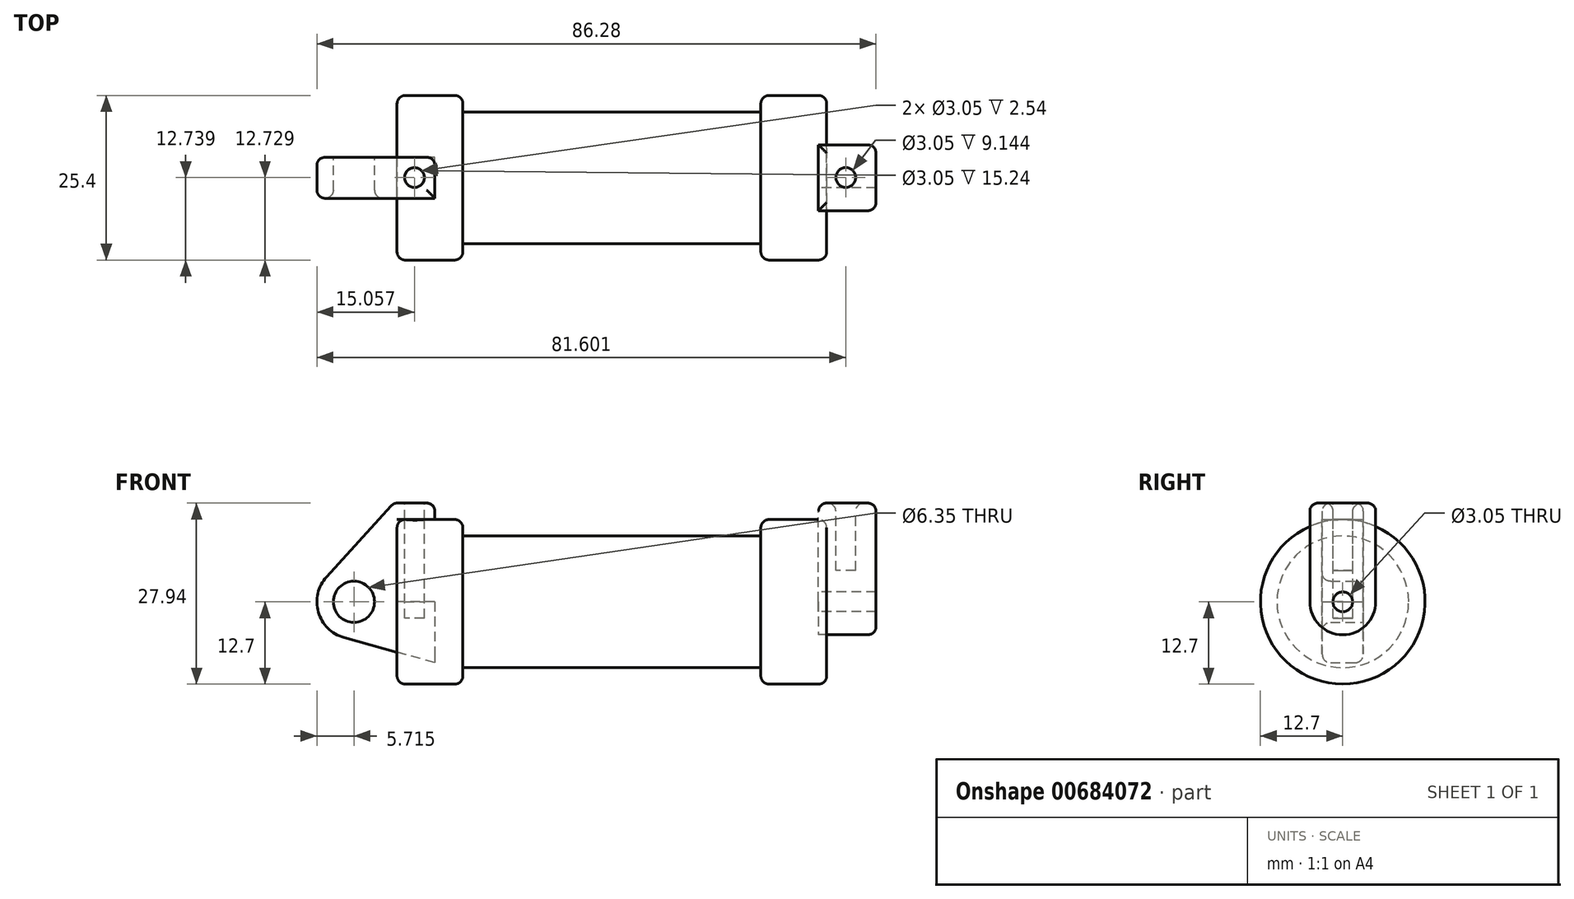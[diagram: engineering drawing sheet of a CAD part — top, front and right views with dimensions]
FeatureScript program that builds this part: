
annotation { "Feature Type Name" : "Feature", "Feature Type Description" : "" }
export const myFeature = defineFeature(function(context is Context, id is Id, definition is map)
    precondition{}
    {
        {
            var Q0;
            Q0=qCreatedBy(makeId("Front.planeOp"),FACE);
            var sketch = newSketch(context, id + "F0", { "sketchPlane" : qUnion([Q0])});
            skLineSegment(sketch, "E0", {"start": v(0, 0) * mm, "end": v(0, 12.7) * mm});
            skLineSegment(sketch, "E1", {"start": v(0, 12.7) * mm, "end": v(10.16, 12.7) * mm});
            skLineSegment(sketch, "E2", {"start": v(10.16, 12.7) * mm, "end": v(10.16, 10.16) * mm});
            skLineSegment(sketch, "E3", {"start": v(10.16, 10.16) * mm, "end": v(56.13, 10.16) * mm});
            skLineSegment(sketch, "E4", {"start": v(56.13, 10.16) * mm, "end": v(56.13, 12.7) * mm});
            skLineSegment(sketch, "E5", {"start": v(56.13, 12.7) * mm, "end": v(66.3, 12.7) * mm});
            skLineSegment(sketch, "E6", {"start": v(66.3, 12.7) * mm, "end": v(66.3, 0) * mm});
            skLineSegment(sketch, "E7", {"start": v(66.3, 0) * mm, "end": v(0, 0) * mm});
            skLineSegment(sketch, "E8", {"start": v(5.84, 15.24) * mm, "end": v(-0.5, 15.24) * mm});
            skLineSegment(sketch, "E9", {"start": v(-0.5, 15.24) * mm, "end": v(-10.88, 3.85) * mm});
            skLineSegment(sketch, "E10", {"start": v(0, 0) * mm, "end": v(-6.65, 0) * mm});
            skCircle(sketch, "E11", {"center": v(-6.65, 0) * mm, "radius": 5.72 * mm});
            skCircle(sketch, "E12", {"center": v(-6.65, 0) * mm, "radius": 3.18 * mm});
            skLineSegment(sketch, "E13", {"start": v(5.84, 15.24) * mm, "end": v(5.84, -9.4) * mm});
            skLineSegment(sketch, "E14", {"start": v(5.84, -9.4) * mm, "end": v(-8.18, -5.5) * mm});
            skText(sketch, "E15", { "text": "volume\n1.706 ^3", "fontName": "OpenSans-Regular.ttf"});
            const initialGuessF0  = {"E15": [0.00013, 0.0607, 1, 0, 0.01304]};
            skSetInitialGuess(sketch, initialGuessF0);
            skSolve(sketch);
        }
        {
            var Q0;
            {var subQ0=sQuery(id+"F0.wireOp",EDGE,"E2");Q0=makeQuery(id+"F0.imprint","IMPRINT",FACE,{"disambiguationData":[TD([[makeQuery(id+"F0.imprint","IMPRINT",EDGE,{"derivedFrom":subQ0}),-1.0]])]});}
            var Q1;
            {var subQ0=sQuery(id+"F0.wireOp",EDGE,"E0");Q1=makeQuery(id+"F0.imprint","IMPRINT",FACE,{"disambiguationData":[TD([[makeQuery(id+"F0.imprint","IMPRINT",EDGE,{"derivedFrom":subQ0}),-1.0]])]});}
            var Q2;
            Q2=sQuery(id+"F0.wireOp",EDGE,"E7");
            revolve(context, id + "F1", {"entities" : qUnion([Q0, Q1]), "axis" : qUnion([Q2]), "revolveType" : RevolveType.FULL});
        }
        {
            var Q0;
            {var subQ1=sQuery(id+"F0.wireOp",EDGE,"E0");Q0=makeQuery(id+"F0.imprint","IMPRINT",FACE,{"disambiguationData":[TD([[makeQuery(id+"F0.imprint","IMPRINT",EDGE,{"derivedFrom":subQ1}),1.0]])]});}
            var Q1;
            {var subQ0=sQuery(id+"F0.wireOp",EDGE,"E14");Q1=makeQuery(id+"F0.imprint","IMPRINT",FACE,{"disambiguationData":[TD([[makeQuery(id+"F0.imprint","IMPRINT",EDGE,{"derivedFrom":subQ0}),-1.0]])]});}
            var Q2;
            {var subQ5=sQuery(id+"F0.wireOp",EDGE,"E12");Q2=makeQuery(id+"F0.imprint","IMPRINT",FACE,{"disambiguationData":[TD([[makeQuery(id+"F0.imprint","IMPRINT",EDGE,{"derivedFrom":subQ5}),-1.0]])]});}
            extrude(context, id + "F2", {"entities" : qUnion([Q0, Q1, Q2]), "endBound" : BoundingType.SYMMETRIC, "depth" : 6.35 * mm, "offsetDistance" : 25.4 * mm});
        }
        {
            var Q0;
            Q0=makeQuery(id+"F1.opRevolve","SWEPT_FACE",FACE,{"disambiguationData":[OSD([sQuery(id+"F0.wireOp",EDGE,"E6")])]});
            var sketch = newSketch(context, id + "F3", { "sketchPlane" : qUnion([Q0])});
            skCircle(sketch, "E16", {"center": v(0, 0) * mm, "radius": 1.52 * mm});
            skCircle(sketch, "E17", {"center": v(0, 0) * mm, "radius": 5.08 * mm});
            skLineSegment(sketch, "E18", {"start": v(-5.08, 0) * mm, "end": v(-5.08, 15.24) * mm});
            skLineSegment(sketch, "E19", {"start": v(5.08, 0) * mm, "end": v(5.08, 15.24) * mm});
            skLineSegment(sketch, "E20", {"start": v(-5.08, 15.24) * mm, "end": v(5.08, 15.24) * mm});
            skSolve(sketch);
        }
        {
            var Q0;
            Q0 = qSketchRegion(id + "F3", true);
            extrude(context, id + "F4", {"entities" : qUnion([Q0]), "depth" : 7.62 * mm, "offsetDistance" : 25.4 * mm, "hasSecondDirection" : true, "secondDirectionOppositeDirection" : true, "secondDirectionDepth" : 1.27 * mm});
        }
        {
            var Q0;
            Q0=makeQuery(id+"F4.opExtrude","SWEPT_FACE",FACE,{"disambiguationData":[OSD([sQuery(id+"F3.wireOp",EDGE,"E20")])]});
            var sketch = newSketch(context, id + "F5", { "sketchPlane" : qUnion([Q0])});
            skCircle(sketch, "E21", {"center": v(69.23, 0.04) * mm, "radius": 1.52 * mm});
            skSolve(sketch);
        }
        {
            var Q0;
            Q0=makeQuery(id+"F5.imprint","IMPRINT",FACE,{"disambiguationData":[TD([[makeQuery(id+"F5.imprint","IMPRINT",EDGE,{"derivedFrom":sQuery(id+"F5.wireOp",EDGE,"E21")}),1.0]])]});
            extrude(context, id + "F6", {"entities" : qUnion([Q0]), "operationType" : NewBodyOperationType.REMOVE, "oppositeDirection" : true, "depth" : 10.4 * mm, "offsetDistance" : 25.4 * mm});
        }
        {
            var Q0;
            Q0=makeQuery(id+"F2.opExtrude","SWEPT_FACE",FACE,{"disambiguationData":[OSD([sQuery(id+"F0.wireOp",EDGE,"E8")])]});
            var sketch = newSketch(context, id + "F7", { "sketchPlane" : qUnion([Q0])});
            skCircle(sketch, "E22", {"center": v(2.69, 0.03) * mm, "radius": 1.52 * mm});
            skSolve(sketch);
        }
        {
            var Q0;
            Q0=makeQuery(id+"F7.imprint","IMPRINT",FACE,{"disambiguationData":[TD([[makeQuery(id+"F7.imprint","IMPRINT",EDGE,{"derivedFrom":sQuery(id+"F7.wireOp",EDGE,"E22")}),1.0]])]});
            extrude(context, id + "F8", {"entities" : qUnion([Q0]), "operationType" : NewBodyOperationType.REMOVE, "oppositeDirection" : true, "depth" : 17.78 * mm, "offsetDistance" : 25.4 * mm});
        }
        {
            var Q0;
            Q0=makeQuery(id+"F1.opRevolve","SWEPT_EDGE",EDGE,{"disambiguationData":[OSD([sQuery(id+"F0.wireOp",EDGE,"E1"),sQuery(id+"F0.wireOp",EDGE,"E2")])]});
            var Q1;
            Q1=makeQuery(id+"F1.opRevolve","SWEPT_EDGE",EDGE,{"disambiguationData":[OSD([sQuery(id+"F0.wireOp",EDGE,"E0"),sQuery(id+"F0.wireOp",EDGE,"E1")])]});
            var Q2;
            Q2=makeQuery(id+"F2.opExtrude","CAP_EDGE",EDGE,{"disambiguationData":[OSD([sQuery(id+"F0.wireOp",EDGE,"E8")])],"isStart":false});
            var Q3;
            {var subQ0=sQuery(id+"F0.wireOp",EDGE,"E13");Q3=makeQuery(id+"F2.opExtrude","CAP_EDGE",EDGE,{"disambiguationData":[OSD([subQ0]),TDD([makeQuery(id+"F0.imprint","IMPRINT",EDGE,{"disambiguationData":[TD([[makeQuery(id+"F0.imprint","INTERSECT",VERTEX,{"derivedFrom":[sQuery(id+"F0.wireOp",EDGE,"E8"),subQ0]}),-1.0]])],"derivedFrom":subQ0})])],"isStart":true});}
            var Q4;
            Q4=makeQuery(id+"F2.opExtrude","SWEPT_EDGE",EDGE,{"disambiguationData":[OSD([sQuery(id+"F0.wireOp",EDGE,"E8"),sQuery(id+"F0.wireOp",EDGE,"E9")])]});
            var Q5;
            Q5=makeQuery(id+"F2.opExtrude","CAP_EDGE",EDGE,{"disambiguationData":[OSD([sQuery(id+"F0.wireOp",EDGE,"E8")])],"isStart":true});
            var Q6;
            Q6=makeQuery(id+"F2.opExtrude","SWEPT_FACE",FACE,{"disambiguationData":[OSD([sQuery(id+"F0.wireOp",EDGE,"E9")])]});
            var Q7;
            Q7=makeQuery(id+"F2.opExtrude","CAP_EDGE",EDGE,{"disambiguationData":[OSD([sQuery(id+"F0.wireOp",EDGE,"E12")])],"isStart":false});
            var Q8;
            Q8=makeQuery(id+"F2.opExtrude","SWEPT_EDGE",EDGE,{"disambiguationData":[OSD([sQuery(id+"F0.wireOp",EDGE,"E8"),sQuery(id+"F0.wireOp",EDGE,"E13")])]});
            var Q9;
            Q9=makeQuery(id+"F4.opExtrude","CAP_EDGE",EDGE,{"disambiguationData":[OSD([sQuery(id+"F3.wireOp",EDGE,"E19")])],"isStart":false});
            var Q10;
            Q10=makeQuery(id+"F4.opExtrude","CAP_EDGE",EDGE,{"disambiguationData":[OSD([sQuery(id+"F3.wireOp",EDGE,"E20")])],"isStart":false});
            var Q11;
            Q11=makeQuery(id+"F4.opExtrude","SWEPT_FACE",FACE,{"disambiguationData":[OSD([sQuery(id+"F3.wireOp",EDGE,"E20")])]});
            var Q12;
            Q12=makeQuery(id+"F1.opRevolve","SWEPT_FACE",FACE,{"disambiguationData":[OSD([sQuery(id+"F0.wireOp",EDGE,"E6")])]});
            var Q13;
            Q13=makeQuery(id+"F1.opRevolve","SWEPT_EDGE",EDGE,{"disambiguationData":[OSD([sQuery(id+"F0.wireOp",EDGE,"E4"),sQuery(id+"F0.wireOp",EDGE,"E5")])]});
            fillet(context, id + "F9", {"entities" : qUnion([Q0, Q1, Q2, Q3, Q4, Q5, Q6, Q7, Q8, Q9, Q10, Q11, Q12, Q13]), "radius" : 1.27 * mm, "tangentPropagation" : true, "allowEdgeOverflow" : false});
        }
    });
